# Revit family: Toilet_Elongated-Right_Height-American_Standard-H2OPTION-2886.X18_Series
name_source: partatom
category: Plumbing Fixtures
units: mm (PartAtom-declared; Revit-internal decimal feet)

## family parameters
Always vertical = No
Cut with Voids When Loaded = No
OmniClass Number = 23.45.05.21.11.11
OmniClass Title = Water Operated Water Closets
Part Type = Normal
Room Calculation Point = No
Round Connector Dimension = Use Radius
Shared = Yes
Work Plane-Based = Yes

## types (6) — shared parameters
ADA Compliant = Yes
ASME A112.19.2/CSA B45.1 = Yes
Assembly Code = D2010110
Bowl Shape = Elongated
CW Connection = Yes
CWFU = 10
CalGreen Compliant = Yes
Cold Water Connection Diameter = 1/2"
Cold Water Connection Height = 10"
Cold Water Connection Radius = 1/4"
Cold Water Connection Width = 6"
Default Elevation = 0"
Description = H2Option Dual Flush Right Height Elongated Toilet.
EPA WaterSense® Certified = Yes
Flush Rate = (Full Flush - 4.8 Lpf/1.28gpf) or (Partial Flush - 3.4 Lpf/0.92 gpf)
HW Connection = No
Height = 31 1/2"
Installation Type = Floor Mounted
Length = 29 3/4"
Manufacturer = American Standard
Price = Prices may vary. Please consult Manufacturer Representative for most up-to-date price list.
Product Documentation Link = https://americanstandard.box.com
Product Page URL = https://www.americanstandard-us.com
Push Button Finish = Metal-American Standard-Chrome Plated
Revised Date = 01/24/2022
URL = http://www.americanstandard-us.com
Vent Connection = No
WFU = 10
Warranty Information = Limited lifetime warranty on chinaware and limited five year warranty on all mechanical parts
Waste Connection = Yes
Waste Connection Diameter = 2"
Waste Connection Radius = 1"
Width = 15"
zero-valued in all types: HWFU

## per-type parameters (varying)
| type | Aquaguard Liner | Finish | Material |
| 2886.218.020 | No | Vitreous China-American Standard-020-White | Vitreous China-American Standard-020-White |
| 2886.518.020 | Yes | Vitreous China-American Standard-020-White | Vitreous China-American Standard-020-White |
| 2886.218.222 | No | Vitreous China-American Standard-222-Linen | Vitreous China-American Standard-222-Linen |
| 2886.218.021 | No | Vitreous China-American Standard-021-Bone | Vitreous China-American Standard-021-Bone |
| 2886.518.021 | Yes | Vitreous China-American Standard-021-Bone | Vitreous China-American Standard-021-Bone |
| 2886.518.222 | Yes | Vitreous China-American Standard-222-Linen | Vitreous China-American Standard-222-Linen |

note: column(s) folded — value = type name in every type: Model

## geometry (parser evidence)
native form markers: Sweep x2
no freeform markers — native parametric forms only
